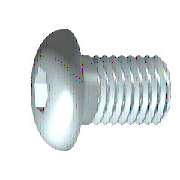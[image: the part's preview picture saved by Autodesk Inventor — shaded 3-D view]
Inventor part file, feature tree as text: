
AUTODESK INVENTOR PART (.ipt)
format: ipt  version: 2025 (Build 290162010, 162A)  size: 198,656 bytes
history: native  units: mm (DEFAULTED — no unit token found)
features: extrude x1, plane x1, fillet x1
ambient origin geometry x7: Origin, YZ Plane, XY Plane, X Axis, Y Axis, Z Axis, Center Point
bodies: Solid1 (feature_tree), Body (feature_tree)
feature tree (3):
  extrude  "Slot"  Depth=10.5mm
  plane  "Work Plane1"
  fillet  "Fillet2"  Radius=0.306825mm
